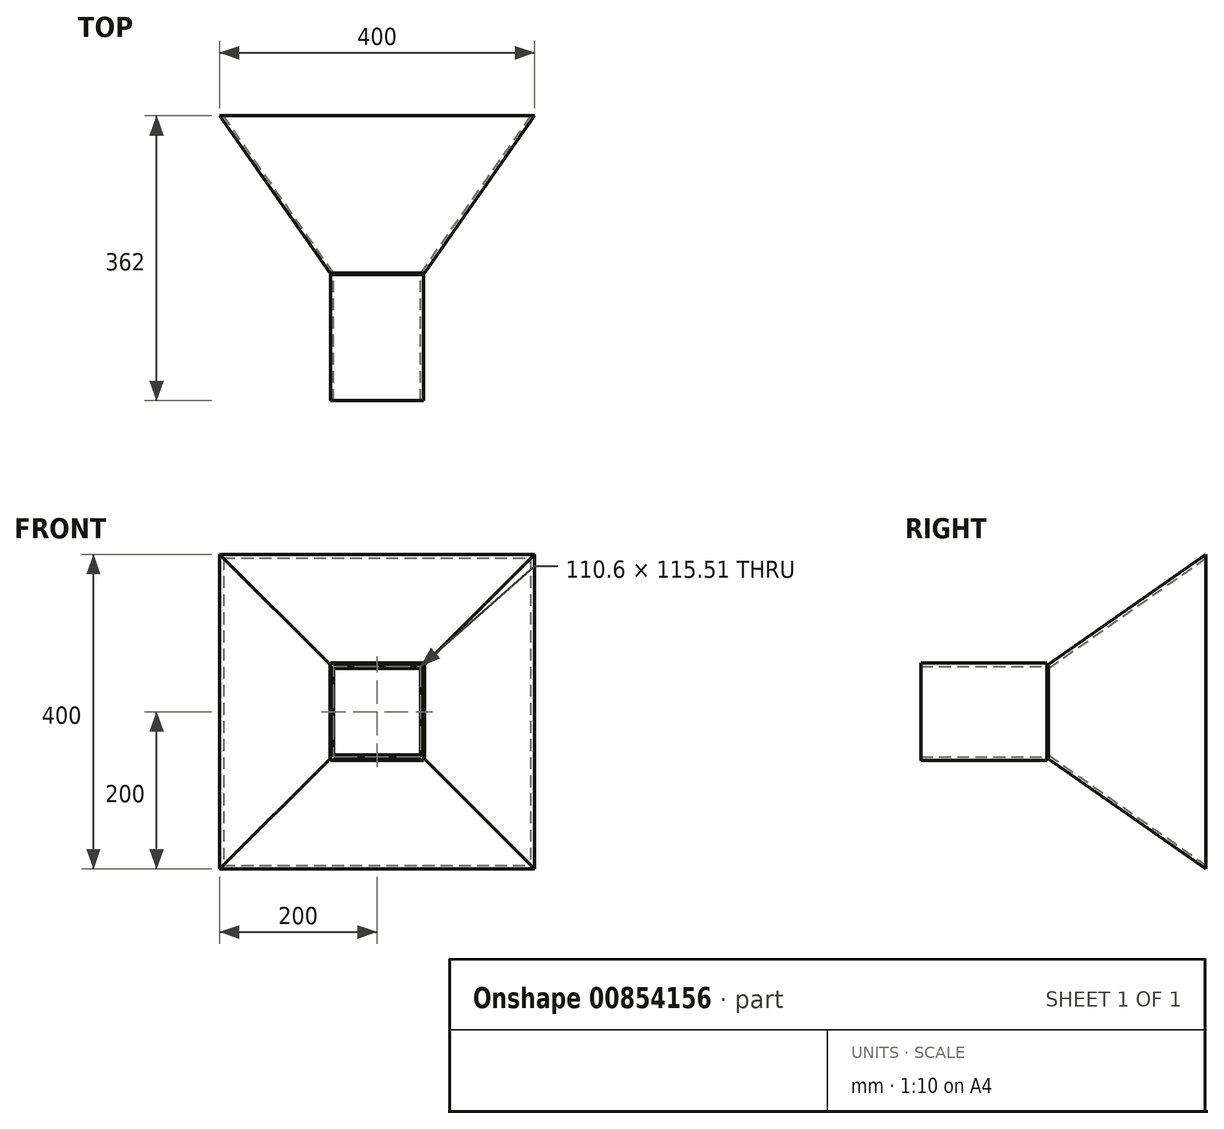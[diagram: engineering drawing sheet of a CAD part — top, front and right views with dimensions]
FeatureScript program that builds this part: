
annotation { "Feature Type Name" : "Feature", "Feature Type Description" : "" }
export const myFeature = defineFeature(function(context is Context, id is Id, definition is map)
    precondition{}
    {
        {
            var Q0;
            Q0=qCreatedBy(makeId("Front.planeOp"),FACE);
            var sketch = newSketch(context, id + "F0", { "sketchPlane" : qUnion([Q0])});
            skLineSegment(sketch, "E0.bottom", {"start": v(-200, 200) * mm, "end": v(200, 200) * mm});
            skLineSegment(sketch, "E0.top", {"start": v(-200, -200) * mm, "end": v(200, -200) * mm});
            skLineSegment(sketch, "E0.left", {"start": v(-200, 200) * mm, "end": v(-200, -200) * mm});
            skLineSegment(sketch, "E0.right", {"start": v(200, 200) * mm, "end": v(200, -200) * mm});
            skPoint(sketch, "E0.middle", {"position": v(0, 0) * mm});
            skSolve(sketch);
        }
        {
            var Q0;
            Q0=makeQuery(id+"F0.imprint","IMPRINT",FACE,{"disambiguationData":[TD([[makeQuery(id+"F0.imprint","IMPRINT",EDGE,{"derivedFrom":sQuery(id+"F0.wireOp",EDGE,"E0.bottom")}),-1.0]])]});
            cPlane(context, id + "F1", {"entities" : qUnion([Q0]), "cplaneType" : CPlaneType.OFFSET, "offset" : 200 * mm, "width" : 150 * mm, "height" : 150 * mm});
        }
        {
            var Q0;
            Q0=qCreatedBy(id+"F1.planeOp",FACE);
            var sketch = newSketch(context, id + "F2", { "sketchPlane" : qUnion([Q0])});
            skLineSegment(sketch, "E1.bottom", {"start": v(-60, 60) * mm, "end": v(60, 60) * mm});
            skLineSegment(sketch, "E1.top", {"start": v(-60, -60) * mm, "end": v(60, -60) * mm});
            skLineSegment(sketch, "E1.left", {"start": v(-60, 60) * mm, "end": v(-60, -60) * mm});
            skLineSegment(sketch, "E1.right", {"start": v(60, 60) * mm, "end": v(60, -60) * mm});
            skPoint(sketch, "E1.middle", {"position": v(0, 0) * mm});
            skSolve(sketch);
        }
        {
            var Q0;
            Q0=makeQuery(id+"F0.imprint","IMPRINT",FACE,{"disambiguationData":[TD([[makeQuery(id+"F0.imprint","IMPRINT",EDGE,{"derivedFrom":sQuery(id+"F0.wireOp",EDGE,"E0.bottom")}),-1.0]])]});
            var Q1;
            Q1=makeQuery(id+"F2.imprint","IMPRINT",FACE,{"disambiguationData":[TD([[makeQuery(id+"F2.imprint","IMPRINT",EDGE,{"derivedFrom":sQuery(id+"F2.wireOp",EDGE,"E1.bottom")}),-1.0]])]});
            loft(context, id + "F3", {"sheetProfilesArray" : [{ "sheetProfileEntities" : qUnion([Q0]) }, { "sheetProfileEntities" : qUnion([Q1]) }]});
        }
        {
            var Q0;
            Q0=makeQuery(id+"F3.opLoft","CAP_FACE",FACE,{"disambiguationData":[OSD([makeQuery(id+"F0.imprint","IMPRINT",FACE,{"disambiguationData":[TD([[makeQuery(id+"F0.imprint","IMPRINT",EDGE,{"derivedFrom":sQuery(id+"F0.wireOp",EDGE,"E0.bottom")}),-1.0]])]})])],"isStart":true});
            var Q1;
            Q1=makeQuery(id+"F3.opLoft","CAP_FACE",FACE,{"disambiguationData":[OSD([makeQuery(id+"F2.imprint","IMPRINT",FACE,{"disambiguationData":[TD([[makeQuery(id+"F2.imprint","IMPRINT",EDGE,{"derivedFrom":sQuery(id+"F2.wireOp",EDGE,"E1.bottom")}),-1.0]])]})])],"isStart":true});
            shell(context, id + "F4", {"entities" : qUnion([Q0, Q1]), "thickness" : 4 * mm});
        }
        {
            var Q0;
            Q0=qCreatedBy(makeId("Front.planeOp"),FACE);
            cPlane(context, id + "F5", {"entities" : qUnion([Q0]), "cplaneType" : CPlaneType.OFFSET, "offset" : 202 * mm, "width" : 150 * mm, "height" : 150 * mm});
        }
        {
            var Q0;
            Q0=qCreatedBy(id+"F5.planeOp",FACE);
            var sketch = newSketch(context, id + "F6", { "sketchPlane" : qUnion([Q0])});
            skLineSegment(sketch, "E2.bottom", {"start": v(-59.3, 61.76) * mm, "end": v(59.3, 61.76) * mm});
            skLineSegment(sketch, "E2.top", {"start": v(-59.3, -61.76) * mm, "end": v(59.3, -61.76) * mm});
            skLineSegment(sketch, "E2.left", {"start": v(-59.3, 61.76) * mm, "end": v(-59.3, -61.76) * mm});
            skLineSegment(sketch, "E2.right", {"start": v(59.3, 61.76) * mm, "end": v(59.3, -61.76) * mm});
            skPoint(sketch, "E2.middle", {"position": v(0, 0) * mm});
            skLineSegment(sketch, "E3.0", {"start": v(-55.3, 57.76) * mm, "end": v(55.3, 57.76) * mm});
            skLineSegment(sketch, "E3.1", {"start": v(-55.3, 57.76) * mm, "end": v(-55.3, -57.76) * mm});
            skLineSegment(sketch, "E3.2", {"start": v(-55.3, -57.76) * mm, "end": v(55.3, -57.76) * mm});
            skLineSegment(sketch, "E3.3", {"start": v(55.3, 57.76) * mm, "end": v(55.3, -57.76) * mm});
            skLineSegment(sketch, "E4.0", {"start": v(-59.3, 56.76) * mm, "end": v(59.3, 56.76) * mm});
            skSolve(sketch);
        }
        {
            var Q0;
            Q0 = qSketchRegion(id + "F6", true);
            extrude(context, id + "F7", {"entities" : qUnion([Q0]), "depth" : 160 * mm, "offsetDistance" : 25 * mm});
        }
    });
